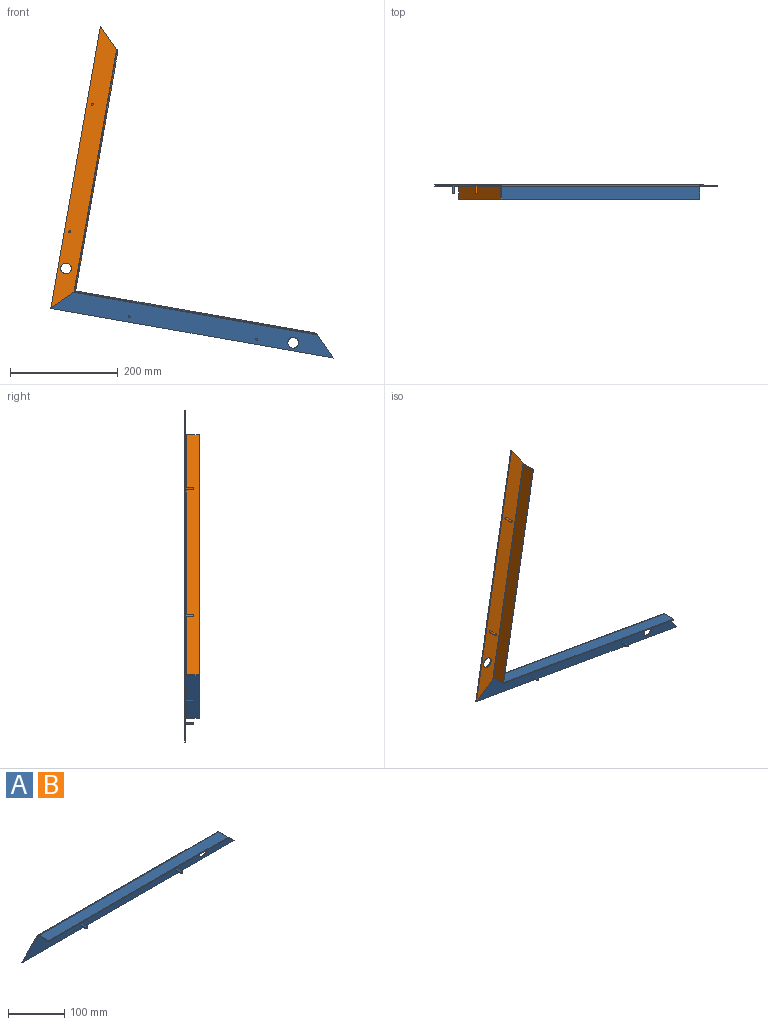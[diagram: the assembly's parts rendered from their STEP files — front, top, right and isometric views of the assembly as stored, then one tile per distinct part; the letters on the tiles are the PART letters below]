
ASSEMBLY  parts=2 mates=1
PART A: 19 faces, bbox 532x27.4x40 mm
  f0: plane 532x37mm, normal (0,-1,0), area 17975.7mm2, adj f3,f7,f8,f12,f14,f16,f18
  f1: plane 532x37mm, normal (0,1,0), area 18000.8mm2, adj f2,f7,f8,f12,f18
  f2: cylinder r=3mm len=458mm, axis (-1,0,0), area 2140.3mm2, adj f1,f4,f10,f13
  f3: cylinder r=1mm len=458mm, axis (-1,0,0), area 713.4mm2, adj f0,f5,f10,f13
  f4: plane 452x24mm, normal (0,0,1), area 10848mm2, adj f2,f6,f9,f11
  f5: plane 452x24mm, normal (0,0,-1), area 10848mm2, adj f3,f6,f9,f11
  f6: plane 452x2mm, normal (0,-1,0), area 904mm2, adj f4,f5,f9,f11
  f7: plane 532x2mm, normal (0,0,-1), area 1064mm2, adj f0,f1,f8,f12
  f8: plane 37x37mm, normal (0.71,0,0.71), area 104.7mm2, adj f0,f1,f7,f10
  f9: plane 24x2mm, normal (1,0,0), area 48mm2, adj f4,f5,f6,f10
  f10: bspline ~3.59x3.59mm, area 9.1mm2, adj f2,f3,f8,f9
  f11: plane 24x2mm, normal (-1,0,0), area 48mm2, adj f4,f5,f6,f13
  f12: plane 37x37mm, normal (-0.71,0,0.71), area 104.7mm2, adj f0,f1,f7,f13
  f13: bspline ~3.72x3.59mm, area 9.1mm2, adj f2,f3,f11,f12
  f14: cylinder r=2mm len=15mm, axis (0,1,0), area 188.5mm2, adj f0,f15
  f15: plane 4x4mm, normal (0,-1,0), area 12.6mm2, adj f14
  f16: cylinder r=2mm len=15mm, axis (0,1,0), area 188.5mm2, adj f0,f17
  f17: plane 4x4mm, normal (0,-1,0), area 12.6mm2, adj f16
  f18: cylinder r=10mm len=20mm, axis (0,1,0), area 125.7mm2, adj f0,f1
PART B: same geometry as A
PLACE A rot(axis=(0,1,0),10deg) t=(4.2,-10.96,-2.18)mm fixed
PLACE B rot(axis=(0,1,0),100deg) t=(-195.55,-10.96,282.66)mm
MATE fastened B.f4 <-> A.f11  axis (0.98,0,-0.17) through (-214.94,-25.96,56.6)mm
